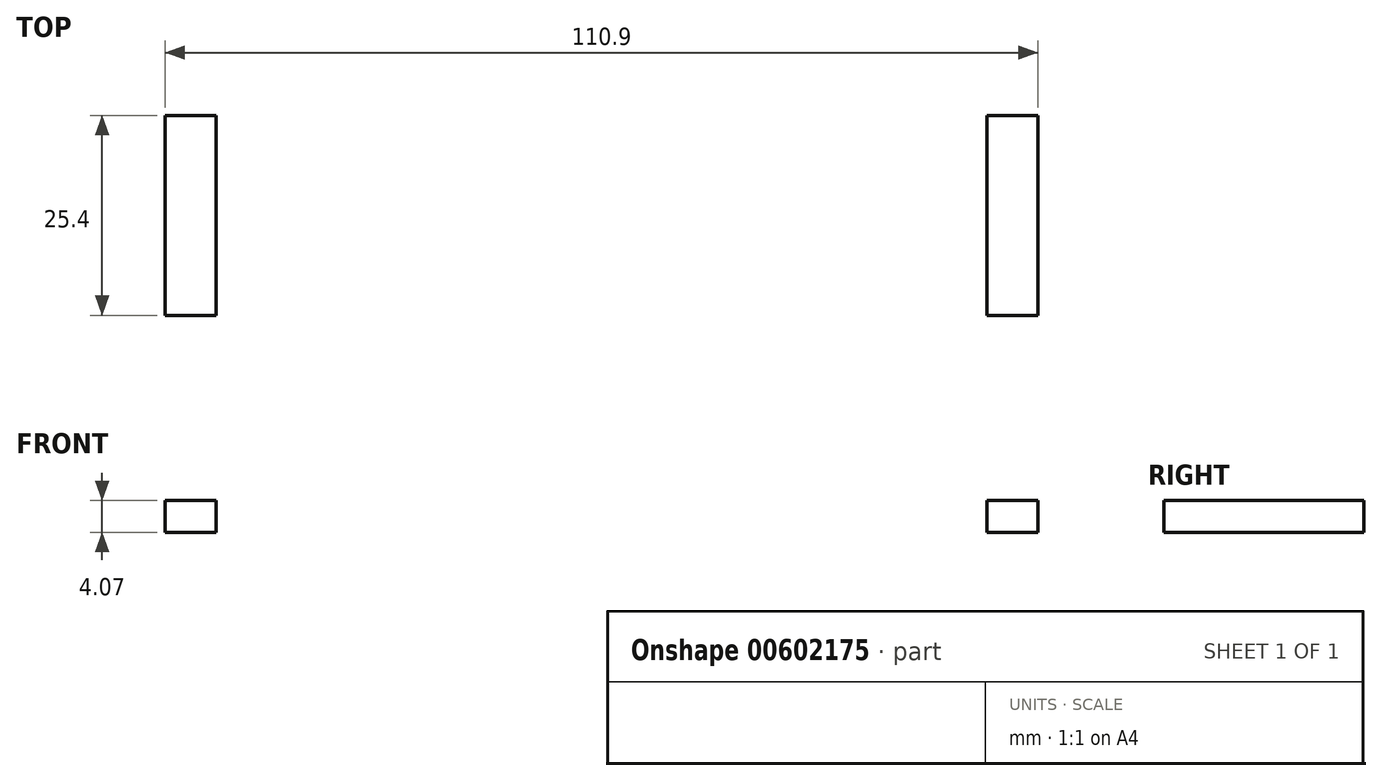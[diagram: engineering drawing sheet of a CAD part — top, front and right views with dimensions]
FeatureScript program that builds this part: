
annotation { "Feature Type Name" : "Feature", "Feature Type Description" : "" }
export const myFeature = defineFeature(function(context is Context, id is Id, definition is map)
    precondition{}
    {
        {
            var Q0;
            Q0=qCreatedBy(makeId("Front.planeOp"),FACE);
            var sketch = newSketch(context, id + "F0", { "sketchPlane" : qUnion([Q0])});
            skLineSegment(sketch, "E0", {"start": v(0, 20.37) * mm, "end": v(0, 0) * mm, "construction": true});
            skLineSegment(sketch, "E1.bottom", {"start": v(-55.45, 0) * mm, "end": v(-48.95, 0) * mm});
            skLineSegment(sketch, "E1.top", {"start": v(-55.45, 4.07) * mm, "end": v(-48.95, 4.07) * mm});
            skLineSegment(sketch, "E1.left", {"start": v(-55.45, 0) * mm, "end": v(-55.45, 4.07) * mm});
            skLineSegment(sketch, "E1.right", {"start": v(-48.95, 0) * mm, "end": v(-48.95, 4.07) * mm});
            skLineSegment(sketch, "E2.MirrorCS", {"start": v(48.95, 0) * mm, "end": v(48.95, 4.07) * mm});
            skLineSegment(sketch, "E3.MirrorCS", {"start": v(55.45, 0) * mm, "end": v(55.45, 4.07) * mm});
            skLineSegment(sketch, "E4.MirrorCS", {"start": v(55.45, 0) * mm, "end": v(48.95, 0) * mm});
            skLineSegment(sketch, "E5.MirrorCS", {"start": v(55.45, 4.07) * mm, "end": v(48.95, 4.07) * mm});
            skSolve(sketch);
        }
        {
            var Q0;
            Q0 = qSketchRegion(id + "F0", true);
            extrude(context, id + "F1", {"entities" : qUnion([Q0]), "depth" : 25.4 * mm, "offsetDistance" : 25.4 * mm});
        }
    });
